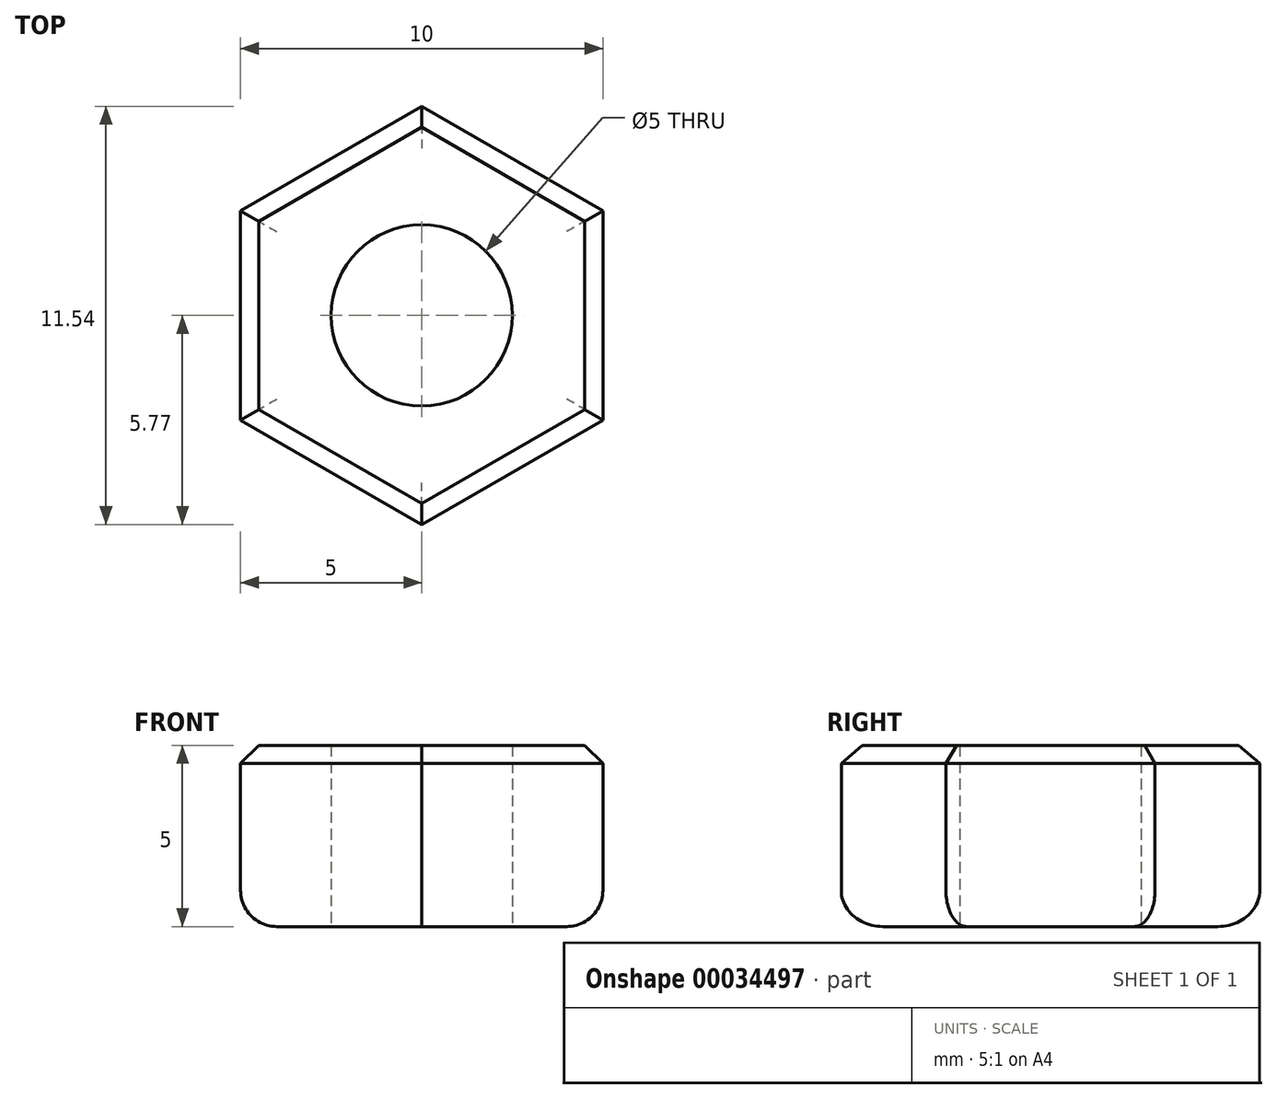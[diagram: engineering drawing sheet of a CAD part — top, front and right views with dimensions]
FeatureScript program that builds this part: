
annotation { "Feature Type Name" : "Feature", "Feature Type Description" : "" }
export const myFeature = defineFeature(function(context is Context, id is Id, definition is map)
    precondition{}
    {
        {
            var Q0;
            Q0=qCreatedBy(makeId("Top.planeOp"),FACE);
            var sketch = newSketch(context, id + "F0", { "sketchPlane" : qUnion([Q0])});
            skCircle(sketch, "E0.cCircle", {"center": v(0, 0) * mm, "radius": 5 * mm, "construction": true});
            skLineSegment(sketch, "E0.0", {"start": v(5, 2.89) * mm, "end": v(5, -2.89) * mm});
            skLineSegment(sketch, "E0.1", {"start": v(5, -2.89) * mm, "end": v(0, -5.77) * mm});
            skLineSegment(sketch, "E0.2", {"start": v(0, -5.77) * mm, "end": v(-5, -2.89) * mm});
            skLineSegment(sketch, "E0.3", {"start": v(-5, -2.89) * mm, "end": v(-5, 2.89) * mm});
            skLineSegment(sketch, "E0.4", {"start": v(-5, 2.89) * mm, "end": v(0, 5.77) * mm});
            skLineSegment(sketch, "E0.5", {"start": v(0, 5.77) * mm, "end": v(5, 2.89) * mm});
            skPoint(sketch, "E0.0.midPoint", {"position": v(5, 0) * mm});
            skCircle(sketch, "E1", {"center": v(0, 0) * mm, "radius": 2.5 * mm});
            skSolve(sketch);
        }
        {
            var Q0;
            Q0 = qSketchRegion(id + "F0", true);
            extrude(context, id + "F1", {"entities" : qUnion([Q0]), "depth" : 5 * mm});
        }
        {
            var Q0;
            Q0=makeQuery(id+"F1.opExtrude","CAP_EDGE",EDGE,{"disambiguationData":[OSD([sQuery(id+"F0.wireOp",EDGE,"E0.2")])],"isStart":true});
            var Q1;
            Q1=makeQuery(id+"F1.opExtrude","CAP_EDGE",EDGE,{"disambiguationData":[OSD([sQuery(id+"F0.wireOp",EDGE,"E0.1")])],"isStart":true});
            var Q2;
            Q2=makeQuery(id+"F1.opExtrude","CAP_EDGE",EDGE,{"disambiguationData":[OSD([sQuery(id+"F0.wireOp",EDGE,"E0.0")])],"isStart":true});
            var Q3;
            Q3=makeQuery(id+"F1.opExtrude","CAP_EDGE",EDGE,{"disambiguationData":[OSD([sQuery(id+"F0.wireOp",EDGE,"E0.5")])],"isStart":true});
            var Q4;
            Q4=makeQuery(id+"F1.opExtrude","CAP_EDGE",EDGE,{"disambiguationData":[OSD([sQuery(id+"F0.wireOp",EDGE,"E0.4")])],"isStart":true});
            var Q5;
            Q5=makeQuery(id+"F1.opExtrude","CAP_EDGE",EDGE,{"disambiguationData":[OSD([sQuery(id+"F0.wireOp",EDGE,"E0.3")])],"isStart":true});
            fillet(context, id + "F2", {"entities" : qUnion([Q0, Q1, Q2, Q3, Q4, Q5]), "radius" : 1 * mm, "tangentPropagation" : true, "allowEdgeOverflow" : false});
        }
        {
            var Q0;
            Q0=makeQuery(id+"F1.opExtrude","CAP_EDGE",EDGE,{"disambiguationData":[OSD([sQuery(id+"F0.wireOp",EDGE,"E0.2")])],"isStart":false});
            var Q1;
            Q1=makeQuery(id+"F1.opExtrude","CAP_EDGE",EDGE,{"disambiguationData":[OSD([sQuery(id+"F0.wireOp",EDGE,"E0.1")])],"isStart":false});
            var Q2;
            Q2=makeQuery(id+"F1.opExtrude","CAP_EDGE",EDGE,{"disambiguationData":[OSD([sQuery(id+"F0.wireOp",EDGE,"E0.0")])],"isStart":false});
            var Q3;
            Q3=makeQuery(id+"F1.opExtrude","CAP_EDGE",EDGE,{"disambiguationData":[OSD([sQuery(id+"F0.wireOp",EDGE,"E0.5")])],"isStart":false});
            var Q4;
            Q4=makeQuery(id+"F1.opExtrude","CAP_EDGE",EDGE,{"disambiguationData":[OSD([sQuery(id+"F0.wireOp",EDGE,"E0.4")])],"isStart":false});
            var Q5;
            Q5=makeQuery(id+"F1.opExtrude","CAP_EDGE",EDGE,{"disambiguationData":[OSD([sQuery(id+"F0.wireOp",EDGE,"E0.3")])],"isStart":false});
            chamfer(context, id + "F3", {"entities" : qUnion([Q0, Q1, Q2, Q3, Q4, Q5]), "width" : 0.5 * mm, "tangentPropagation" : true});
        }
    });
